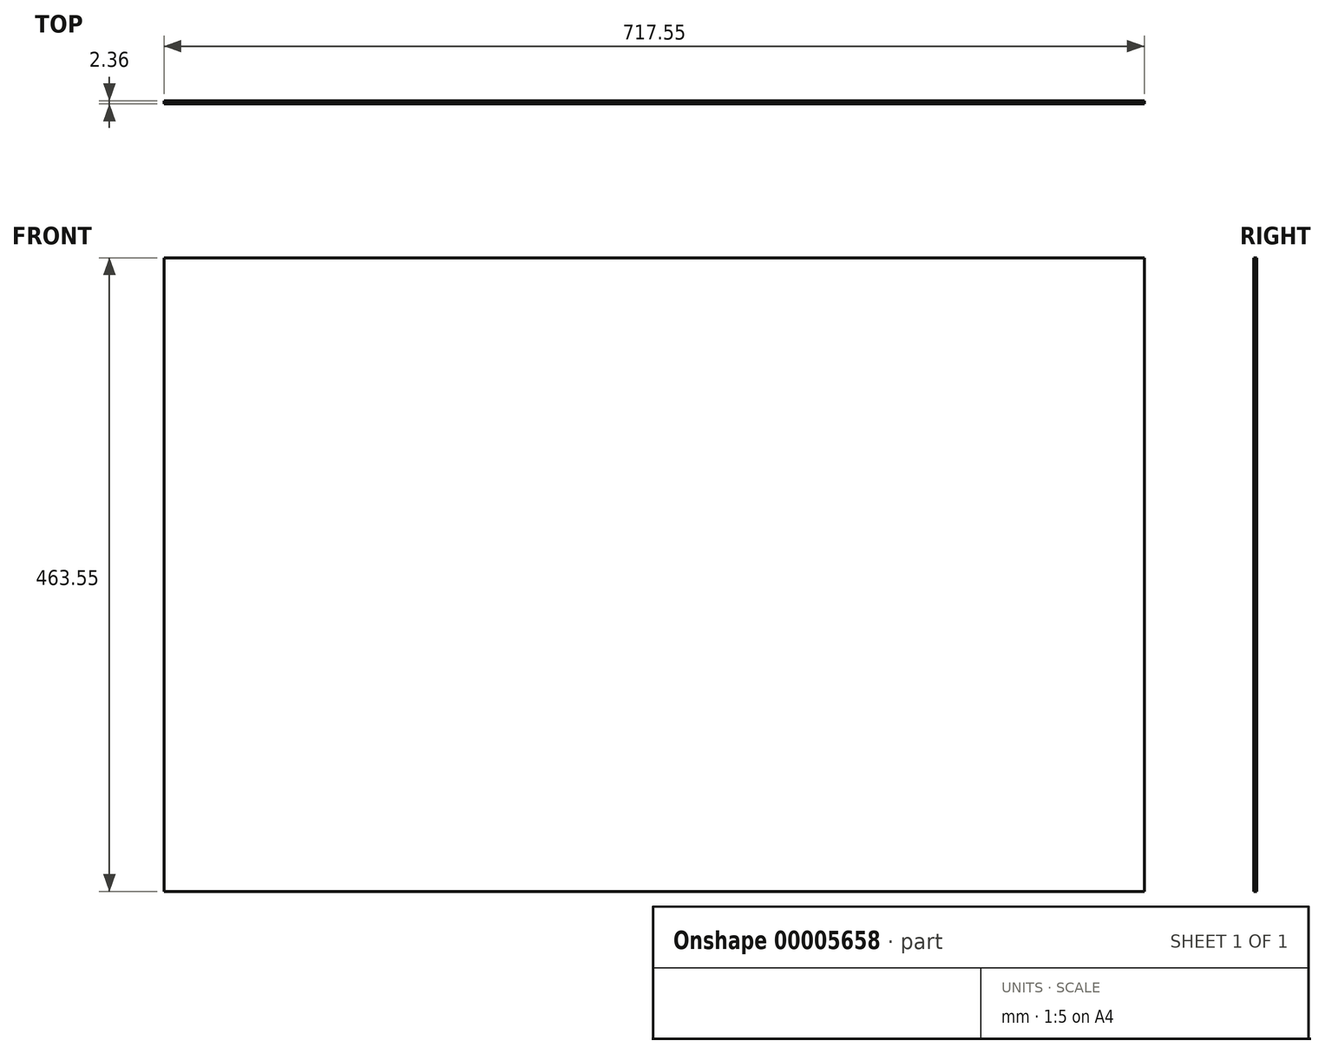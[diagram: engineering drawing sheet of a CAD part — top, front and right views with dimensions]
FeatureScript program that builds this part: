
annotation { "Feature Type Name" : "Feature", "Feature Type Description" : "" }
export const myFeature = defineFeature(function(context is Context, id is Id, definition is map)
    precondition{}
    {
        {
            var Q0;
            Q0=qCreatedBy(makeId("Front.planeOp"),FACE);
            var sketch = newSketch(context, id + "F0", { "sketchPlane" : qUnion([Q0])});
            skLineSegment(sketch, "E0.bottom", {"start": v(0, 0) * mm, "end": v(-717.55, 0) * mm});
            skLineSegment(sketch, "E0.top", {"start": v(0, 463.55) * mm, "end": v(-717.55, 463.55) * mm});
            skLineSegment(sketch, "E0.left", {"start": v(0, 0) * mm, "end": v(0, 463.55) * mm});
            skLineSegment(sketch, "E0.right", {"start": v(-717.55, 0) * mm, "end": v(-717.55, 463.55) * mm});
            skSolve(sketch);
        }
        {
            var Q0;
            Q0 = qSketchRegion(id + "F0", true);
            var Q1;
            Q1=makeQuery(id+"F0.imprint","IMPRINT",FACE,{"disambiguationData":[TD([[makeQuery(id+"F0.imprint","IMPRINT",EDGE,{"derivedFrom":sQuery(id+"F0.wireOp",EDGE,"E0.bottom")}),-1.0]])]});
            extrude(context, id + "F1", {"entities" : qUnion([Q0, Q1]), "depth" : 2.36 * mm});
        }
    });
